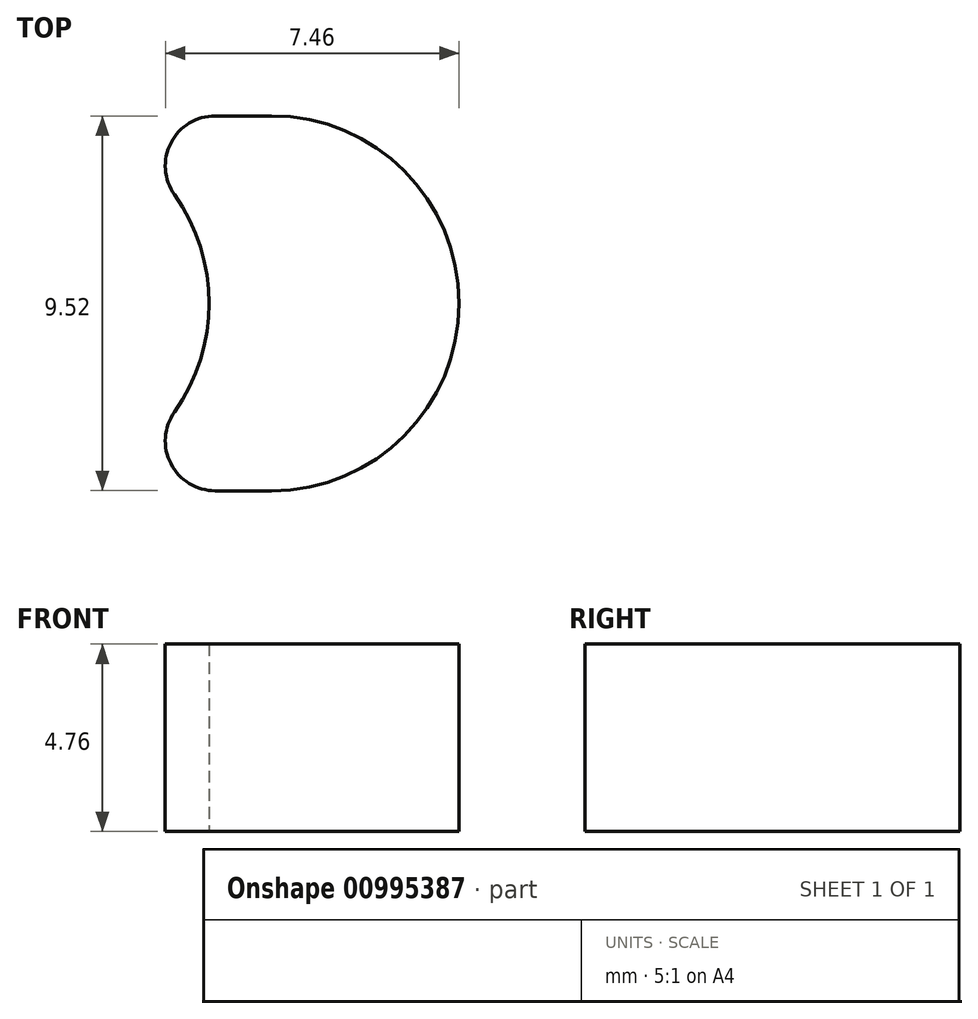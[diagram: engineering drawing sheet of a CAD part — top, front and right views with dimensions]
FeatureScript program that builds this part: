
annotation { "Feature Type Name" : "Feature", "Feature Type Description" : "" }
export const myFeature = defineFeature(function(context is Context, id is Id, definition is map)
    precondition{}
    {
        {
            var Q0;
            Q0=qCreatedBy(makeId("Top.planeOp"),FACE);
            var sketch = newSketch(context, id + "F0", { "sketchPlane" : qUnion([Q0])});
            skArc(sketch, "E0", {"start": v(0, -4.76) * mm, "mid": v(4.76, 0) * mm, "end": v(0, 4.76) * mm});
            skArc(sketch, "E1", {"start": v(6.35, -4.76) * mm, "mid": v(11.11, 0) * mm, "end": v(6.35, 4.76) * mm});
            skLineSegment(sketch, "E2", {"start": v(6.35, -4.76) * mm, "end": v(0, -4.76) * mm});
            skLineSegment(sketch, "E3.MirrorCS", {"start": v(6.35, 4.76) * mm, "end": v(0, 4.76) * mm});
            skSolve(sketch);
        }
        {
            var Q0;
            Q0=makeQuery(id+"F0.imprint","IMPRINT",FACE,{"disambiguationData":[TD([[makeQuery(id+"F0.imprint","IMPRINT",EDGE,{"derivedFrom":sQuery(id+"F0.wireOp",EDGE,"E0")}),-1.0]])]});
            extrude(context, id + "F1", {"entities" : qUnion([Q0]), "depth" : 4.76 * mm, "offsetDistance" : 25.4 * mm});
        }
        {
            var Q0;
            Q0=makeQuery(id+"F1.opExtrude","SWEPT_EDGE",EDGE,{"disambiguationData":[OSD([sQuery(id+"F0.wireOp",EDGE,"E0"),sQuery(id+"F0.wireOp",EDGE,"E2")])]});
            var Q1;
            Q1=makeQuery(id+"F1.opExtrude","SWEPT_EDGE",EDGE,{"disambiguationData":[OSD([sQuery(id+"F0.wireOp",EDGE,"E0"),sQuery(id+"F0.wireOp",EDGE,"E3.MirrorCS")])]});
            fillet(context, id + "F2", {"entities" : qUnion([Q0, Q1]), "radius" : 1.27 * mm, "tangentPropagation" : true, "allowEdgeOverflow" : false});
        }
    });
